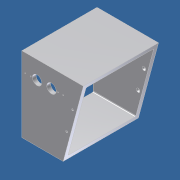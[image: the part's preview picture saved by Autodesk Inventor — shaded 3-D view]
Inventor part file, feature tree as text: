
AUTODESK INVENTOR PART (.ipt)
format: ipt  version: 2012 (Build 160160000, 160)  size: 144,896 bytes
history: native  units: in
note: dims shown in document units (in); Inventor stores cm internally (conversion verified against a paired STEP export)
features: hole x6, sketch x4, pattern_linear x3, extrude x2, fillet x1
ambient origin geometry x8: Origin, YZ Plane, XZ Plane, XY Plane, X Axis, Y Axis, Z Axis, Center Point
bodies: Solid1 (feature_tree)
feature tree (16):
  extrude  "Extrusion1"  Depth=5.5in
  extrude  "Extrusion2"  Depth=0.5in
  sketch  "Sketch6"  dims[d6=8.25in d7=0.0in]
  sketch  "Sketch7"  dims[d8=2.025in d9=7.625in d10=1.25in d11=0.75in d12=1.25in d13=0.25in d14=0.5635in d15=1.0in d16=0.8108in d24=75.0deg d29=3.0in d30=0.5in d31=0.25in d32=0.75in d33=0.5in d34=0.25in d35=0.5635in d36=1.0in d37=0.8108in d38=3.0in d39=0.5in d40=0.25in d41=0.75in d42=0.5in d43=0.25in d44=0.5635in d45=1.0in d46=0.8108in d47=3.0in d48=0.5in d49=0.25in d50=0.75in d51=0.5in d52=0.25in d53=0.5635in d54=1.0in d55=0.8108in d56=3.0in d57=0.5in d58=0.25in d59=0.75in d60=0.5in d61=0.25in d62=0.5635in d63=1.0in d64=0.8108in d65=0.125in d66=0.7874in d68=1.925in d73=3.6875in d74=6.6875in d75=0.5in d76=0.5in d77=1.161in d78=2.375in d79=0.145in d80=0.19in d81=0.375in d82=0.25in d83=0.5635in d84=1.0in d85=0.8108in d86=0.7874in d88=0.7in d90=0.7874in d92=4.35in]
  hole  "Hole1"  [1 undecoded]
  hole  "Hole2"  [1 undecoded]
  hole  "Hole3"  [1 undecoded]
  hole  "Hole4"  [1 undecoded]
  hole  "Hole5"  [1 undecoded]
  fillet  "Fillet1"  Radius=0.5in
  pattern_linear  "Rectangular Pattern2"  Spacing1=0.5in  [1 undecoded]
  hole  "Hole6"  [1 undecoded]
  pattern_linear  "Rectangular Pattern3"  Count1=2 Spacing1=4.35in
  pattern_linear  "Rectangular Pattern4"  [2 undecoded]
  sketch  "Sketch1"  dims[d0=10.0in d2=5.5in]
  sketch  "Sketch2"  dims[d3=10.0in d4=0.0in d5=0.5in]
note: 9 required parameter values undecoded (feature->parameter linkage not recoverable at this tier; creation-order binding heuristic only, values carry confidence <= 0.55)
